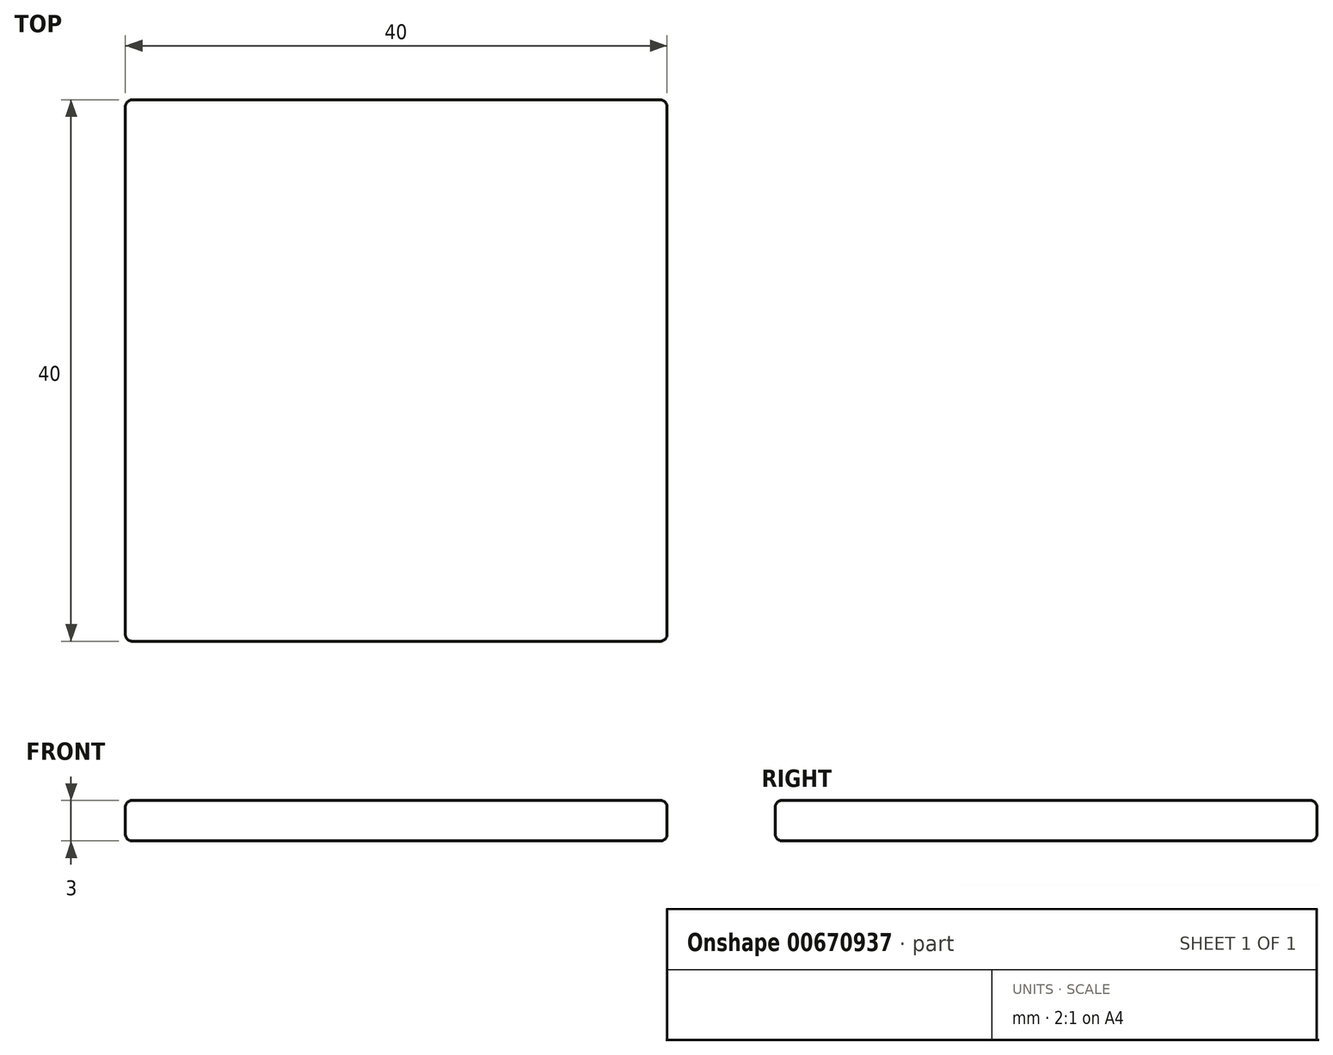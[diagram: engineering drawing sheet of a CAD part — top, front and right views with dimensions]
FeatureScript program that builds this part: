
annotation { "Feature Type Name" : "Feature", "Feature Type Description" : "" }
export const myFeature = defineFeature(function(context is Context, id is Id, definition is map)
    precondition{}
    {
        {
            var Q0;
            Q0=qCreatedBy(makeId("Top.planeOp"),FACE);
            var sketch = newSketch(context, id + "F0", { "sketchPlane" : qUnion([Q0])});
            skLineSegment(sketch, "E0.bottom", {"start": v(-15.77, 24.23) * mm, "end": v(24.23, 24.23) * mm});
            skLineSegment(sketch, "E0.top", {"start": v(-15.77, -15.77) * mm, "end": v(24.23, -15.77) * mm});
            skLineSegment(sketch, "E0.left", {"start": v(-15.77, 24.23) * mm, "end": v(-15.77, -15.77) * mm});
            skLineSegment(sketch, "E0.right", {"start": v(24.23, 24.23) * mm, "end": v(24.23, -15.77) * mm});
            skSolve(sketch);
        }
        {
            var Q0;
            Q0 = qSketchRegion(id + "F0", true);
            extrude(context, id + "F1", {"entities" : qUnion([Q0]), "depth" : 3 * mm, "offsetDistance" : 25 * mm});
        }
        {
            var Q0;
            Q0=makeQuery(id+"F1.opExtrude","CAP_EDGE",EDGE,{"disambiguationData":[OSD([sQuery(id+"F0.wireOp",EDGE,"E0.right")])],"isStart":false});
            var Q1;
            Q1=makeQuery(id+"F1.opExtrude","CAP_EDGE",EDGE,{"disambiguationData":[OSD([sQuery(id+"F0.wireOp",EDGE,"E0.bottom")])],"isStart":false});
            var Q2;
            Q2=makeQuery(id+"F1.opExtrude","CAP_EDGE",EDGE,{"disambiguationData":[OSD([sQuery(id+"F0.wireOp",EDGE,"E0.left")])],"isStart":false});
            var Q3;
            Q3=makeQuery(id+"F1.opExtrude","CAP_EDGE",EDGE,{"disambiguationData":[OSD([sQuery(id+"F0.wireOp",EDGE,"E0.top")])],"isStart":false});
            var Q4;
            Q4=makeQuery(id+"F1.opExtrude","CAP_EDGE",EDGE,{"disambiguationData":[OSD([sQuery(id+"F0.wireOp",EDGE,"E0.right")])],"isStart":true});
            var Q5;
            Q5=makeQuery(id+"F1.opExtrude","CAP_EDGE",EDGE,{"disambiguationData":[OSD([sQuery(id+"F0.wireOp",EDGE,"E0.bottom")])],"isStart":true});
            var Q6;
            Q6=makeQuery(id+"F1.opExtrude","CAP_EDGE",EDGE,{"disambiguationData":[OSD([sQuery(id+"F0.wireOp",EDGE,"E0.left")])],"isStart":true});
            var Q7;
            Q7=makeQuery(id+"F1.opExtrude","CAP_EDGE",EDGE,{"disambiguationData":[OSD([sQuery(id+"F0.wireOp",EDGE,"E0.top")])],"isStart":true});
            var Q8;
            Q8=makeQuery(id+"F1.opExtrude","SWEPT_EDGE",EDGE,{"disambiguationData":[OSD([sQuery(id+"F0.wireOp",EDGE,"E0.bottom"),sQuery(id+"F0.wireOp",EDGE,"E0.left")])]});
            var Q9;
            Q9=makeQuery(id+"F1.opExtrude","SWEPT_EDGE",EDGE,{"disambiguationData":[OSD([sQuery(id+"F0.wireOp",EDGE,"E0.top"),sQuery(id+"F0.wireOp",EDGE,"E0.left")])]});
            var Q10;
            Q10=makeQuery(id+"F1.opExtrude","SWEPT_EDGE",EDGE,{"disambiguationData":[OSD([sQuery(id+"F0.wireOp",EDGE,"E0.bottom"),sQuery(id+"F0.wireOp",EDGE,"E0.right")])]});
            var Q11;
            Q11=makeQuery(id+"F1.opExtrude","SWEPT_EDGE",EDGE,{"disambiguationData":[OSD([sQuery(id+"F0.wireOp",EDGE,"E0.top"),sQuery(id+"F0.wireOp",EDGE,"E0.right")])]});
            fillet(context, id + "F2", {"entities" : qUnion([Q0, Q1, Q2, Q3, Q4, Q5, Q6, Q7, Q8, Q9, Q10, Q11]), "radius" : 0.5 * mm, "tangentPropagation" : true, "allowEdgeOverflow" : false});
        }
    });
